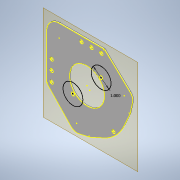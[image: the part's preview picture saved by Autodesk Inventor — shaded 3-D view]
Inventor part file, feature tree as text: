
AUTODESK INVENTOR PART (.ipt)
format: ipt  version: 2022 (Build 260153000, 153)  size: 163,328 bytes
history: native  units: in
note: dims shown in document units (in); Inventor stores cm internally (conversion verified against a paired STEP export)
features: other x3, sketch x2, plane x1, extrude x1, reference x1, projected_geometry x1
ambient origin geometry x8: Origin, YZ Plane, XZ Plane, XY Plane, X Axis, Y Axis, Z Axis, Center Point
bodies: Solid1 (feature_tree)
feature tree (9):
  plane  "Work Plane1"
  extrude  "Extrusion1"  Depth=1.0in
  sketch  "Sketch2"  dims[d2=45.0deg d3=0.1679in d4=0.7874in d6=360.0deg d8=0.0472in d9=0.0in d10=1.0in]
  sketch  "Sketch1"  dims[d0=1.75in d1=1.0in]
  reference  "Reference1"
  projected_geometry  "Projected Loop1"
  other  "<userpath>\Documents\CAD\guardSwerve1\Assembly1.iam"
  other  "Assembly1.iam"
  other  "midblock"
